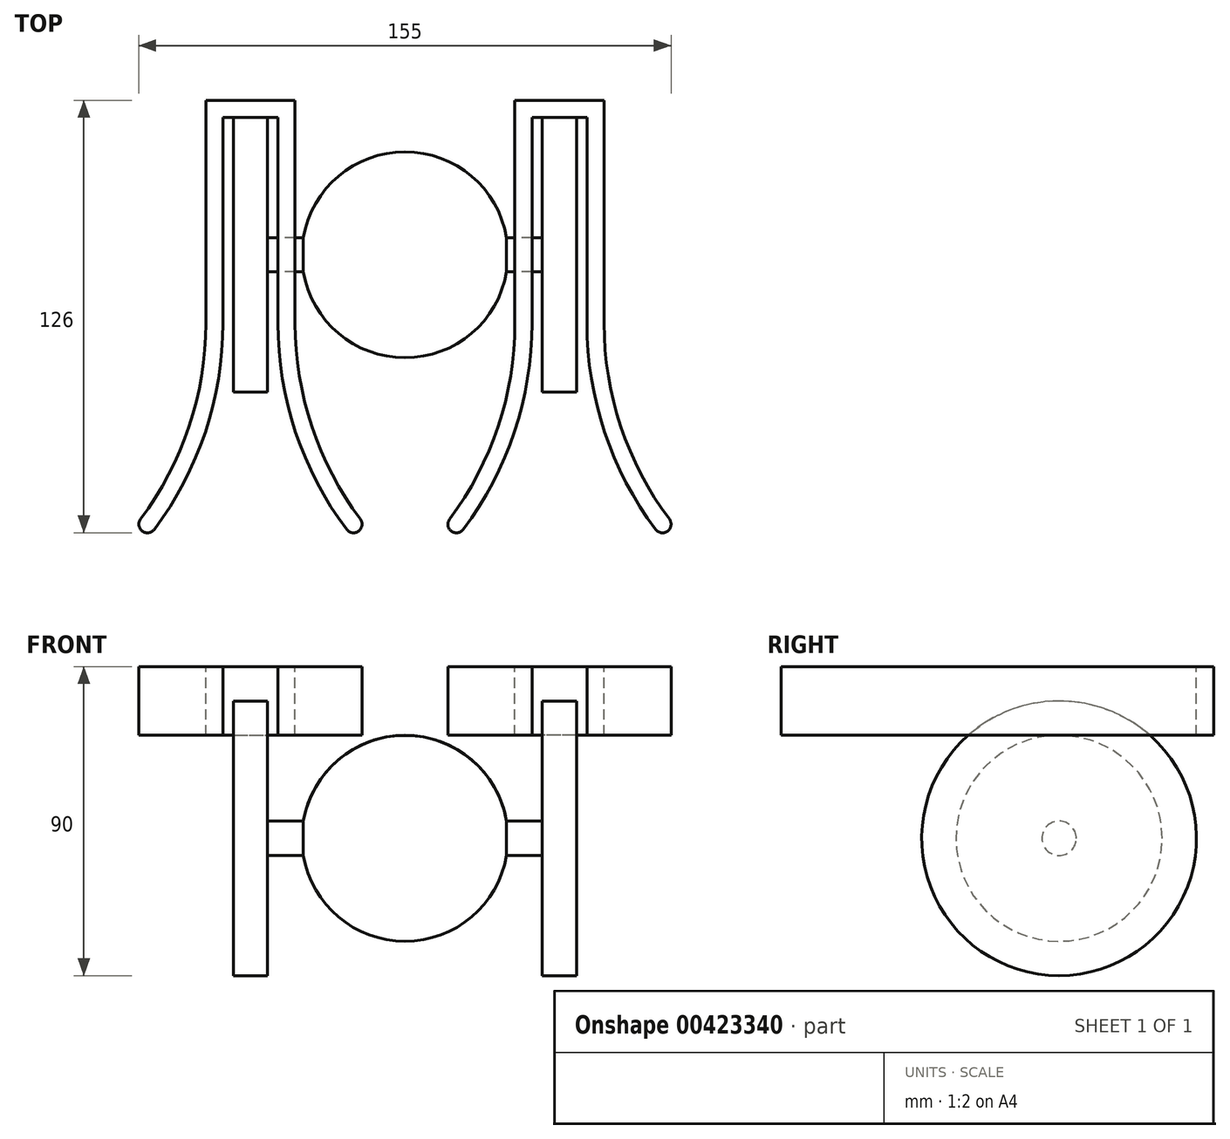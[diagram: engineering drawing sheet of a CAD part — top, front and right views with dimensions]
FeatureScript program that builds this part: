
annotation { "Feature Type Name" : "Feature", "Feature Type Description" : "" }
export const myFeature = defineFeature(function(context is Context, id is Id, definition is map)
    precondition{}
    {
        {
            var Q0;
            Q0=qCreatedBy(makeId("Top.planeOp"),FACE);
            var sketch = newSketch(context, id + "F0", { "sketchPlane" : qUnion([Q0])});
            skArc(sketch, "E0", {"start": v(-29.58, 5) * mm, "mid": v(-19.36, 22.91) * mm, "end": v(0, 30) * mm});
            skLineSegment(sketch, "E1", {"start": v(-50, 0) * mm, "end": v(-50, 40) * mm});
            skLineSegment(sketch, "E2", {"start": v(-50, 40) * mm, "end": v(-40, 40) * mm});
            skLineSegment(sketch, "E3", {"start": v(-40, 40) * mm, "end": v(-40, 5) * mm});
            skLineSegment(sketch, "E4", {"start": v(-40, 5) * mm, "end": v(-29.58, 5) * mm});
            skLineSegment(sketch, "E5", {"start": v(-50, 0) * mm, "end": v(0, 0) * mm});
            skLineSegment(sketch, "E6.MirrorCS", {"start": v(40, 5) * mm, "end": v(29.58, 5) * mm});
            skLineSegment(sketch, "E7.MirrorCS", {"start": v(50, 0) * mm, "end": v(0, 0) * mm});
            skLineSegment(sketch, "E8.MirrorCS", {"start": v(50, 0) * mm, "end": v(50, 40) * mm});
            skLineSegment(sketch, "E9.MirrorCS", {"start": v(50, 40) * mm, "end": v(40, 40) * mm});
            skLineSegment(sketch, "E10.MirrorCS", {"start": v(40, 40) * mm, "end": v(40, 5) * mm});
            skArc(sketch, "E11.MirrorCS", {"start": v(29.58, 5) * mm, "mid": v(19.36, 22.91) * mm, "end": v(0, 30) * mm});
            skSolve(sketch);
        }
        {
            var Q0;
            Q0 = qSketchRegion(id + "F0", true);
            var Q1;
            Q1=sQuery(id+"F0.wireOp",EDGE,"E5");
            revolve(context, id + "F1", {"entities" : qUnion([Q0]), "axis" : qUnion([Q1]), "revolveType" : RevolveType.FULL});
        }
        {
            var Q0;
            Q0=qCreatedBy(makeId("Top.planeOp"),FACE);
            cPlane(context, id + "F2", {"entities" : qUnion([Q0]), "cplaneType" : CPlaneType.OFFSET, "offset" : 50 * mm, "width" : 150 * mm, "height" : 150 * mm});
        }
        {
            var Q0;
            Q0=qCreatedBy(id+"F2.planeOp",FACE);
            var sketch = newSketch(context, id + "F3", { "sketchPlane" : qUnion([Q0])});
            skLineSegment(sketch, "E12.bottom", {"start": v(-53, -20) * mm, "end": v(-37, -20) * mm, "construction": true});
            skLineSegment(sketch, "E12.top", {"start": v(-53, 40) * mm, "end": v(-37, 40) * mm});
            skLineSegment(sketch, "E12.left", {"start": v(-53, -20) * mm, "end": v(-53, 40) * mm});
            skLineSegment(sketch, "E12.right", {"start": v(-37, -20) * mm, "end": v(-37, 40) * mm});
            skLineSegment(sketch, "E13", {"start": v(-53, 0) * mm, "end": v(-50, 0) * mm, "construction": true});
            skLineSegment(sketch, "E14", {"start": v(-40, 0) * mm, "end": v(-37, 0) * mm, "construction": true});
            skArc(sketch, "E15", {"start": v(-53, -20) * mm, "mid": v(-58.13, -51.62) * mm, "end": v(-73, -80) * mm});
            skArc(sketch, "E16", {"start": v(-37, -20) * mm, "mid": v(-31.87, -51.62) * mm, "end": v(-17, -80) * mm});
            skLineSegment(sketch, "E17", {"start": v(-73, -80) * mm, "end": v(-17, -80) * mm, "construction": true});
            skArc(sketch, "E18.0", {"start": v(-58, -20) * mm, "mid": v(-62.88, -50.04) * mm, "end": v(-77, -77) * mm});
            skArc(sketch, "E18.1", {"start": v(-32, -20) * mm, "mid": v(-27.12, -50.04) * mm, "end": v(-13, -77) * mm});
            skLineSegment(sketch, "E18.2", {"start": v(-32, -20) * mm, "end": v(-32, 45) * mm});
            skLineSegment(sketch, "E18.3", {"start": v(-58, 45) * mm, "end": v(-32, 45) * mm});
            skLineSegment(sketch, "E18.4", {"start": v(-58, -20) * mm, "end": v(-58, 45) * mm});
            skLineSegment(sketch, "E19", {"start": v(-77, -77) * mm, "end": v(-73, -80) * mm, "construction": true});
            skLineSegment(sketch, "E20", {"start": v(-17, -80) * mm, "end": v(-13, -77) * mm, "construction": true});
            skArc(sketch, "E21", {"start": v(-77, -77) * mm, "mid": v(-76.5, -80.5) * mm, "end": v(-73, -80) * mm});
            skArc(sketch, "E22", {"start": v(-17, -80) * mm, "mid": v(-13.5, -80.5) * mm, "end": v(-13, -77) * mm});
            skLineSegment(sketch, "E23.MirrorCS", {"start": v(17, -80) * mm, "end": v(13, -77) * mm, "construction": true});
            skLineSegment(sketch, "E24.MirrorCS", {"start": v(77, -77) * mm, "end": v(73, -80) * mm, "construction": true});
            skArc(sketch, "E25.MirrorCS", {"start": v(17, -80) * mm, "mid": v(13.5, -80.5) * mm, "end": v(13, -77) * mm});
            skArc(sketch, "E26.MirrorCS", {"start": v(77, -77) * mm, "mid": v(76.5, -80.5) * mm, "end": v(73, -80) * mm});
            skLineSegment(sketch, "E27.MirrorCS", {"start": v(53, 0) * mm, "end": v(50, 0) * mm, "construction": true});
            skLineSegment(sketch, "E28.MirrorCS", {"start": v(40, 0) * mm, "end": v(37, 0) * mm, "construction": true});
            skArc(sketch, "E29.MirrorCS", {"start": v(37, -20) * mm, "mid": v(31.87, -51.62) * mm, "end": v(17, -80) * mm});
            skLineSegment(sketch, "E30.MirrorCS", {"start": v(37, -20) * mm, "end": v(37, 40) * mm});
            skLineSegment(sketch, "E31.MirrorCS", {"start": v(58, -20) * mm, "end": v(58, 45) * mm});
            skLineSegment(sketch, "E32.MirrorCS", {"start": v(58, 45) * mm, "end": v(32, 45) * mm});
            skArc(sketch, "E33.MirrorCS", {"start": v(53, -20) * mm, "mid": v(58.13, -51.62) * mm, "end": v(73, -80) * mm});
            skArc(sketch, "E34.MirrorCS", {"start": v(58, -20) * mm, "mid": v(62.88, -50.04) * mm, "end": v(77, -77) * mm});
            skLineSegment(sketch, "E35.MirrorCS", {"start": v(73, -80) * mm, "end": v(17, -80) * mm, "construction": true});
            skLineSegment(sketch, "E36.MirrorCS", {"start": v(32, -20) * mm, "end": v(32, 45) * mm});
            skLineSegment(sketch, "E37.MirrorCS", {"start": v(53, -20) * mm, "end": v(37, -20) * mm, "construction": true});
            skLineSegment(sketch, "E38.MirrorCS", {"start": v(53, 40) * mm, "end": v(37, 40) * mm});
            skLineSegment(sketch, "E39.MirrorCS", {"start": v(53, -20) * mm, "end": v(53, 40) * mm});
            skArc(sketch, "E40.MirrorCS", {"start": v(32, -20) * mm, "mid": v(27.12, -50.04) * mm, "end": v(13, -77) * mm});
            skSolve(sketch);
        }
        {
            var Q0;
            Q0 = qSketchRegion(id + "F3", true);
            extrude(context, id + "F4", {"entities" : qUnion([Q0]), "oppositeDirection" : true, "depth" : 20 * mm});
        }
    });
